# Revit family: Furniture_Office-Desks&Tables_Dandent_DTM1152_Computer-Arm_Manual
name_source: partatom
category: Furniture
revit_build: Autodesk Revit 2017 (Build: 20190508_0315(x64)
units: mm (PartAtom-declared; Revit-internal decimal feet)

## family parameters
Cut with Voids When Loaded = No
Host = Face
OmniClass Number = 23.40.70.11.14.21
OmniClass Title = Health Care Furniture
Room Calculation Point = No
Shared = No

## types (1)
- Manual computer arm - DTM1152
    ArmMainMaterial = White steel
    AssetType = Fixed
    BIMObjectName = Furniture_Office-Desks&Tables_Dandent_DTM1152_Computer-Arm_Manual
    Brand = Dandent
    Category = Computer furniture
    Color = White
    ConvergoRefNr = 0151-1909-0010-SE
    Default Elevation = 0 mm  [stored 0 ft]
    DurationUnit = Year
    Features = Pre-assembled cable channels
    Finish = Table available in white, birch or beech laminate
    IfcExportAs = IfcFurnitureType
    IfcExportType = UNDEFINED
    MainColor = White
    Manufacturer = Dandent
    ManufacturerName = Dandent
    ManufacturerURL = https://www.dandent.se
    Material = Steel, wood, plastic
    Model = Manual computer arm - DTM1152
    ModelNumber = DTM1152
    NBSDescription = Medical desks, tables and worktops
    NBSReference = 45-35-80/380
    Name = Dandent_DTM1152_Computer-Arm_Manual
    NominalDepth = 1016 mm
    NominalHeight = 1053 mm
    NominalLength = 650 mm
    Product data url = https://www.bimobject.com
    ProductDatasheet = https://www.dandent.se
    Shape = Sculptured
    Size = 650x1010x1050 mm
    URL = https://www.dandent.se
    Uniclass2 = Pr_40_50
    Uniclass2015Description = Medical desks, tables and worktops
    Uniclass2015Reference = Pr_40_50_52
    Version = 1
    VersionDate = 12/09/2019
    WarrantyDurationUnit = Year

note: [stored X ft] marks values corroborated as IEEE doubles in the binary element streams (Revit-internal decimal feet)

## geometry (parser evidence)
native form markers: Sweep x6
no freeform markers — native parametric forms only
